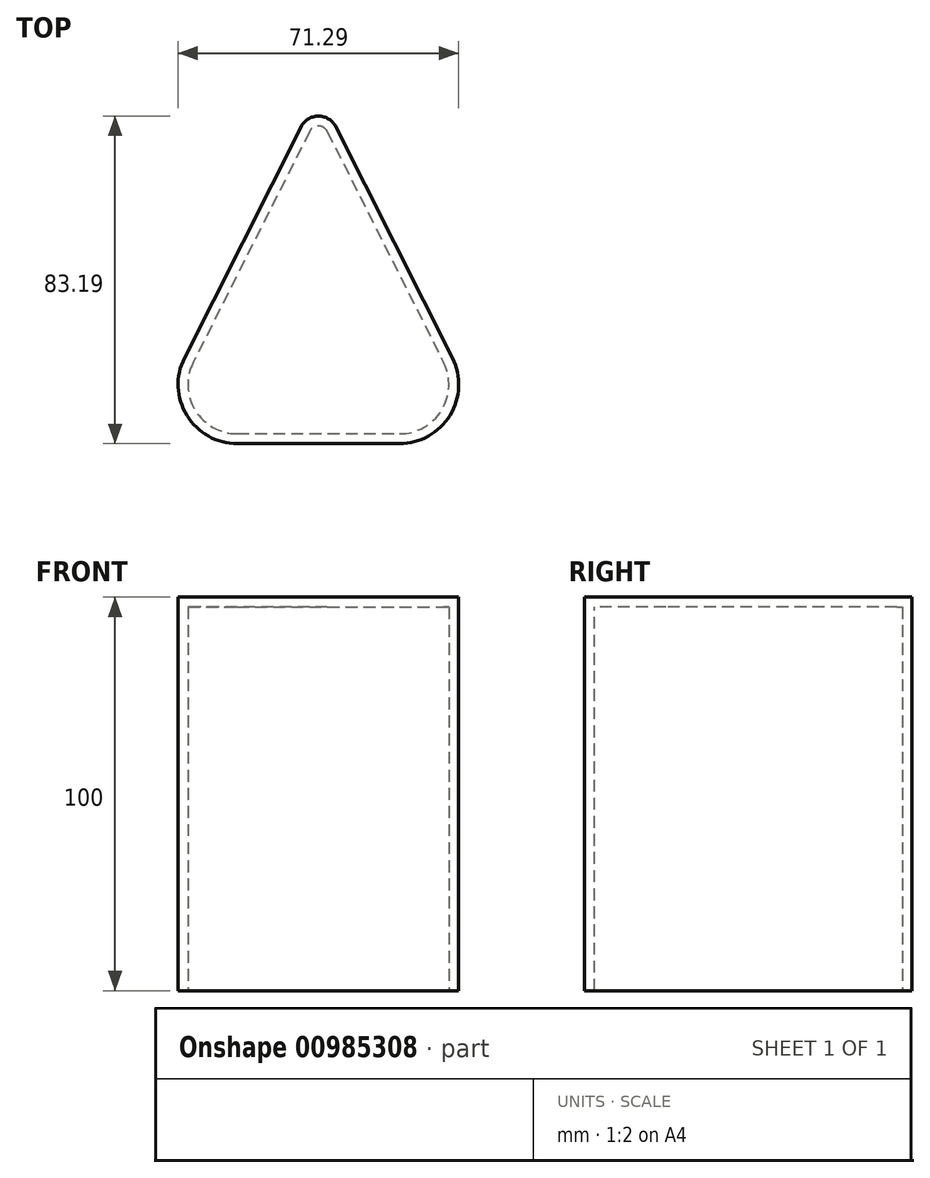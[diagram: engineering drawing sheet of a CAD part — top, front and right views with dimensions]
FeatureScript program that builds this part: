
annotation { "Feature Type Name" : "Feature", "Feature Type Description" : "" }
export const myFeature = defineFeature(function(context is Context, id is Id, definition is map)
    precondition{}
    {
        {
            var Q0;
            Q0=qCreatedBy(makeId("Top.planeOp"),FACE);
            var sketch = newSketch(context, id + "F0", { "sketchPlane" : qUnion([Q0])});
            skLineSegment(sketch, "E0", {"start": v(-9.93, 80.44) * mm, "end": v(-39.5, 21.75) * mm});
            skLineSegment(sketch, "E1", {"start": v(-1, 80.44) * mm, "end": v(28.58, 21.75) * mm});
            skLineSegment(sketch, "E2", {"start": v(-26.1, 0) * mm, "end": v(15.18, 0) * mm});
            skPoint(sketch, "E3.visualSharp", {"position": v(-5.46, 89.3) * mm});
            skArc(sketch, "E3.filletArc", {"start": v(-1, 80.44) * mm, "mid": v(-5.46, 83.2) * mm, "end": v(-9.93, 80.44) * mm});
            skPoint(sketch, "E4.visualSharp", {"position": v(-50.46, 0) * mm});
            skArc(sketch, "E4.filletArc", {"start": v(-39.5, 21.75) * mm, "mid": v(-38.88, 7.13) * mm, "end": v(-26.1, 0) * mm});
            skPoint(sketch, "E5.visualSharp", {"position": v(39.54, 0) * mm});
            skArc(sketch, "E5.filletArc", {"start": v(15.18, 0) * mm, "mid": v(27.95, 7.13) * mm, "end": v(28.58, 21.75) * mm});
            skSolve(sketch);
        }
        {
            var Q0;
            Q0=makeQuery(id+"F0.imprint","IMPRINT",FACE,{"disambiguationData":[TD([[makeQuery(id+"F0.imprint","IMPRINT",EDGE,{"derivedFrom":sQuery(id+"F0.wireOp",EDGE,"E0")}),1.0]])]});
            extrude(context, id + "F1", {"entities" : qUnion([Q0]), "depth" : 100 * mm, "offsetDistance" : 25 * mm});
        }
        {
            var Q0;
            Q0=makeQuery(id+"F1.opExtrude","CAP_FACE",FACE,{"disambiguationData":[OSD([sQuery(id+"F0.wireOp",EDGE,"E0"),sQuery(id+"F0.wireOp",EDGE,"E1"),sQuery(id+"F0.wireOp",EDGE,"E2"),sQuery(id+"F0.wireOp",EDGE,"E3.filletArc"),sQuery(id+"F0.wireOp",EDGE,"E4.filletArc"),sQuery(id+"F0.wireOp",EDGE,"E5.filletArc")])],"isStart":true});
            shell(context, id + "F2", {"entities" : qUnion([Q0]), "thickness" : 2.5 * mm});
        }
    });
